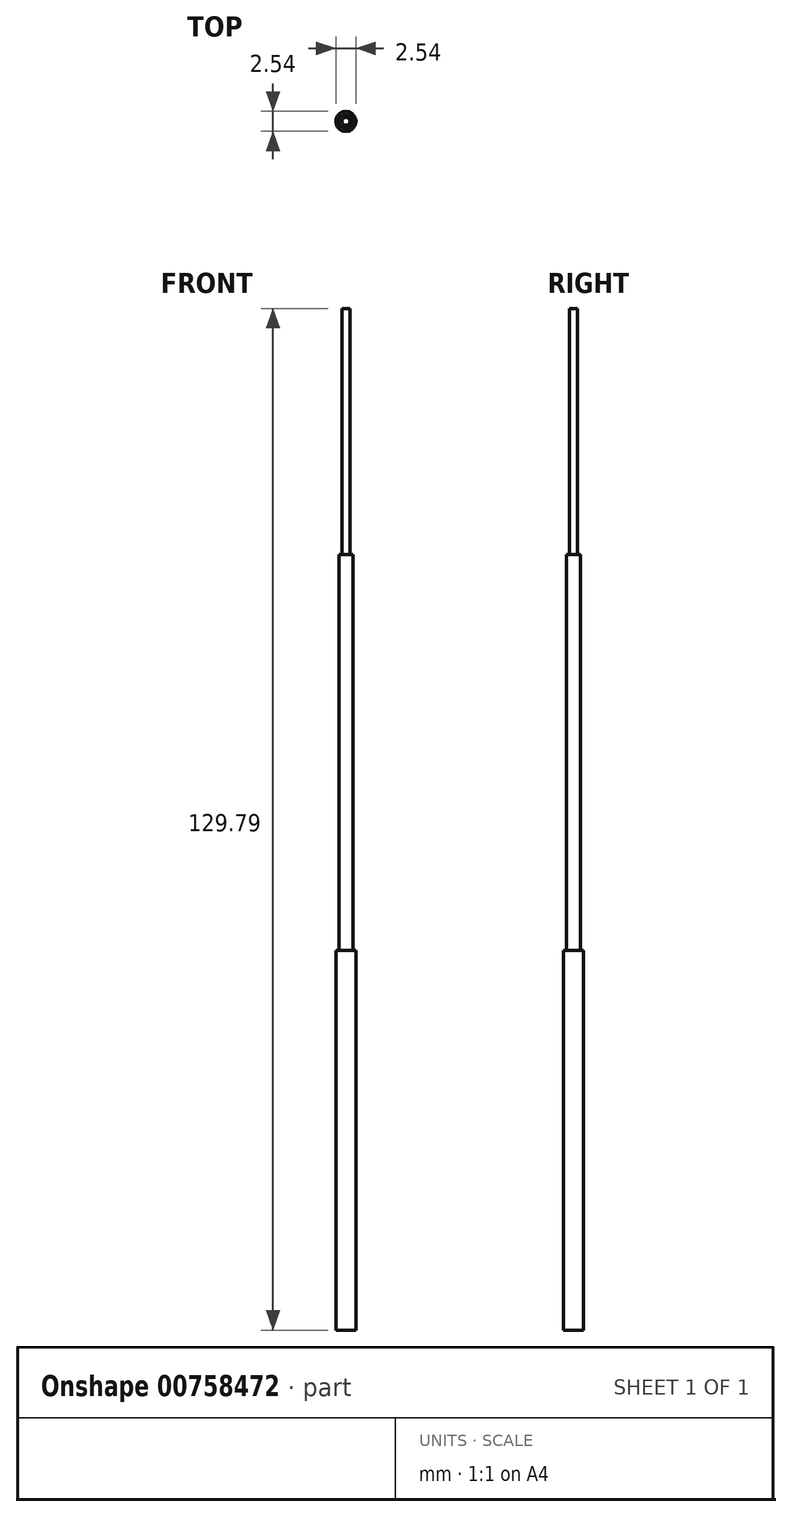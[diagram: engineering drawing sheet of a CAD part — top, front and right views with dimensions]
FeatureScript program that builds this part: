
annotation { "Feature Type Name" : "Feature", "Feature Type Description" : "" }
export const myFeature = defineFeature(function(context is Context, id is Id, definition is map)
    precondition{}
    {
        {
            var Q0;
            Q0=qCreatedBy(makeId("Top.planeOp"),FACE);
            var sketch = newSketch(context, id + "F0", { "sketchPlane" : qUnion([Q0])});
            skCircle(sketch, "E0", {"center": v(0, 0) * mm, "radius": 1.27 * mm});
            skSolve(sketch);
        }
        {
            var Q0;
            Q0 = qSketchRegion(id + "F0", true);
            extrude(context, id + "F1", {"entities" : qUnion([Q0]), "depth" : 48.26 * mm, "offsetDistance" : 25.4 * mm});
        }
        {
            var Q0;
            Q0=qCreatedBy(makeId("Top.planeOp"),FACE);
            var sketch = newSketch(context, id + "F2", { "sketchPlane" : qUnion([Q0])});
            skCircle(sketch, "E1", {"center": v(0, 0) * mm, "radius": 0.89 * mm});
            skSolve(sketch);
        }
        {
            var Q0;
            Q0 = qSketchRegion(id + "F2", true);
            extrude(context, id + "F3", {"entities" : qUnion([Q0]), "operationType" : NewBodyOperationType.ADD, "depth" : 98.55 * mm, "offsetDistance" : 25.4 * mm});
        }
        {
            var Q0;
            Q0=qCreatedBy(makeId("Top.planeOp"),FACE);
            var sketch = newSketch(context, id + "F4", { "sketchPlane" : qUnion([Q0])});
            skCircle(sketch, "E2", {"center": v(0, 0) * mm, "radius": 0.5 * mm});
            skSolve(sketch);
        }
        {
            var Q0;
            Q0 = qSketchRegion(id + "F4", true);
            extrude(context, id + "F5", {"entities" : qUnion([Q0]), "operationType" : NewBodyOperationType.ADD, "depth" : 129.8 * mm, "offsetDistance" : 25.4 * mm});
        }
    });
